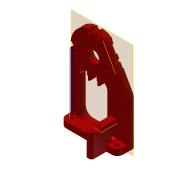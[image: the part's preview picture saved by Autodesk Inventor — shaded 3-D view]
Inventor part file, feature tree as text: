
AUTODESK INVENTOR PART (.ipt)
format: ipt  version: 2015 SP2 (Build 190223200, 223)  size: 532,480 bytes
history: native  units: mm
features: sketch x26, extrude x25, projected_geometry x8, plane x7, fillet x5, reference x4, other x1, mirror x1, hole x1, chamfer x1
ambient origin geometry x8: Origin, YZ Plane, XZ Plane, XY Plane, X Axis, Y Axis, Z Axis, Center Point
bodies: Body1 (feature_tree)
feature tree (79):
  other  "Sólido1"
  extrude  "Extrusión1"  Depth=29.0mm
  extrude  "Extrusión2"  Depth=11.0mm
  extrude  "Extrusión3"  Depth=15.0mm
  fillet  "Empalme1"  Radius=49.5mm
  extrude  "Extrusión4"  Depth=154.0mm TaperAngle=0.0deg
  extrude  "Extrusión5"  Depth=20.8mm
  fillet  "Empalme2"  Radius=27.5mm
  extrude  "Extrusión6"  Depth=8.0mm
  fillet  "Empalme3"  Radius=8.0mm
  extrude  "Extrusión7"  Depth=5.0mm
  extrude  "Extrusión8"  Depth=11.0mm
  extrude  "Extrusión9"  Depth=4.0mm
  extrude  "Extrusión10"  Depth=2.5mm
  extrude  "Extrusión11"  Depth=44.0mm TaperAngle=0.0deg
  plane  "Plano de trabajo1"
  mirror  "Simetría1"
  extrude  "Extrusión12"  Depth=11.0mm
  hole  "Agujero1"  [1 undecoded]
  extrude  "Extrusión15"  Depth=14.7mm TaperAngle=0.0deg
  plane  "Plano de trabajo2"
  plane  "Plano de trabajo3"
  extrude  "Extrusión16"  Depth=12.5mm
  extrude  "Extrusión13"  Depth=10.0mm
  extrude  "Extrusión14"  Depth=12.5mm
  extrude  "Extrusión17"  Depth=2.5mm
  plane  "Plano de trabajo4"
  extrude  "Extrusión18"  Depth=5.0mm
  plane  "Plano de trabajo5"
  extrude  "Extrusión19"  Depth=5.0mm
  plane  "Plano de trabajo6"
  extrude  "Extrusión20"  Depth=20.0mm TaperAngle=0.0deg
  extrude  "Extrusión21"  Depth=20.0mm TaperAngle=0.0deg
  extrude  "Extrusión22"  Depth=31.5mm
  extrude  "Extrusión23"  Depth=20.0mm
  extrude  "Extrusión24"  Depth=8.0mm
  chamfer  "Chaflán1"  Distance=20.0mm
  plane  "Plano de trabajo7"
  extrude  "Extrusión25"  Depth=0.5mm TaperAngle=0.0deg
  fillet  "Empalme4"  Radius=6.235mm
  fillet  "Empalme5"  Radius=2.79mm
  sketch  "Boceto1"  dims[d0=29.0mm d1=99.5mm]
  sketch  "Boceto2"  dims[d2=10.0mm d3=0.0mm d4=11.0mm]
  sketch  "Boceto3"  dims[d5=144.0mm d6=0.0mm d7=15.0mm d8=49.5mm]
  sketch  "Boceto4"  dims[d9=76.5mm d10=154.0mm d11=0.0mm]
  sketch  "Boceto5"  dims[d12=13.0mm d13=20.8mm d14=27.5mm]
  sketch  "Boceto6"  dims[d15=154.0mm d16=0.0mm d17=22.5mm d18=8.0mm d19=0.0mm]
  sketch  "Boceto7"  dims[d20=10.0mm d21=5.0mm]
  projected_geometry  "Contorno proyectado1"
  sketch  "Boceto8"  dims[d22=40.0mm d23=11.0mm]
  projected_geometry  "Contorno proyectado2"
  sketch  "Boceto9"  dims[d24=44.0mm d25=0.0mm d26=4.0mm]
  projected_geometry  "Contorno proyectado3"
  sketch  "Boceto10"  dims[d27=2.5mm d28=3.0mm]
  projected_geometry  "Contorno proyectado4"
  sketch  "Boceto11"  dims[d29=5.0mm d30=44.0mm d31=0.0mm]
  sketch  "Boceto12"  dims[d32=11.0mm d33=3.5mm]
  sketch  "Boceto13"  dims[d34=3.5mm d35=5.25mm]
  sketch  "Boceto14"  dims[d36=14.5mm d37=14.7mm d38=0.0mm]
  sketch  "Boceto15"  dims[d39=8.6mm d40=12.5mm]
  sketch  "Boceto16"  dims[d41=20.0mm d42=0.0mm d43=10.0mm]
  sketch  "Boceto17"  dims[d44=20.0mm d45=0.0mm d46=12.5mm]
  projected_geometry  "Contorno proyectado5"
  sketch  "Boceto18"  dims[d47=6.0mm d48=2.5mm]
  projected_geometry  "Contorno proyectado6"
  projected_geometry  "Contorno proyectado7"
  sketch  "Boceto19"  dims[d49=2.5mm d50=5.0mm]
  sketch  "Boceto20"  dims[d51=5.0mm d52=21.5mm]
  sketch  "Boceto22"  dims[d53=5.75mm d54=20.0mm d55=0.0mm]
  sketch  "Boceto25"  dims[d57=78.75mm d58=20.0mm d59=0.0mm]
  projected_geometry  "Contorno proyectado8"
  sketch  "Boceto26"  dims[d60=50.0mm d61=31.5mm]
  reference  "Referencia1"
  reference  "Referencia2"
  sketch  "Boceto27"  dims[d62=9.5mm d63=20.0mm]
  sketch  "Boceto28"  dims[d64=3.5mm d65=6.0mm d66=4.0mm d67=2.0mm d68=90.0deg d69=8.0mm d70=20.594885mm d71=8.6mm d72=20.0mm d73=0.0mm]
  sketch  "Boceto30"  dims[d74=8.6mm d75=20.0mm d76=0.0mm d77=6.235mm d78=2.79mm d79=0.0mm d80=3.75mm d81=3.75mm d82=14.5mm d86=14.7mm d87=0.0mm d88=17.5mm d89=17.5mm d90=3.75mm d91=3.75mm d92=14.5mm d93=14.7mm d94=0.0mm d95=-6.21mm d96=6.235mm d97=6.235mm d98=6.0mm d99=6.0mm d100=2.9mm d101=0.0mm d102=-6.21mm d103=6.235mm d104=6.235mm d105=6.0mm d106=6.0mm d108=2.8mm d109=0.0mm d110=-6.21mm d111=6.235mm d113=6.235mm d114=6.0mm d115=6.0mm d116=2.8mm d117=0.0mm d118=40.5mm d119=1.5mm d120=0.0mm d121=3.4mm d122=3.4mm d123=17.0mm d124=0.0mm d125=14.0mm d126=4.0mm d127=3.0mm d128=0.0mm d129=9.0mm d130=4.0mm d131=7.0mm d132=3.0mm d133=0.0mm d134=0.8mm d135=2.0mm d136=30.0deg d137=-2.6mm d138=6.235mm d139=6.235mm d140=2.0mm d141=2.0mm d142=2.8mm d143=0.0mm d144=0.5mm d145=0.5mm]
  reference  "Referencia3"
  reference  "Referencia4"
note: 1 required parameter value undecoded (feature->parameter linkage not recoverable at this tier; creation-order binding heuristic only, values carry confidence <= 0.55)
